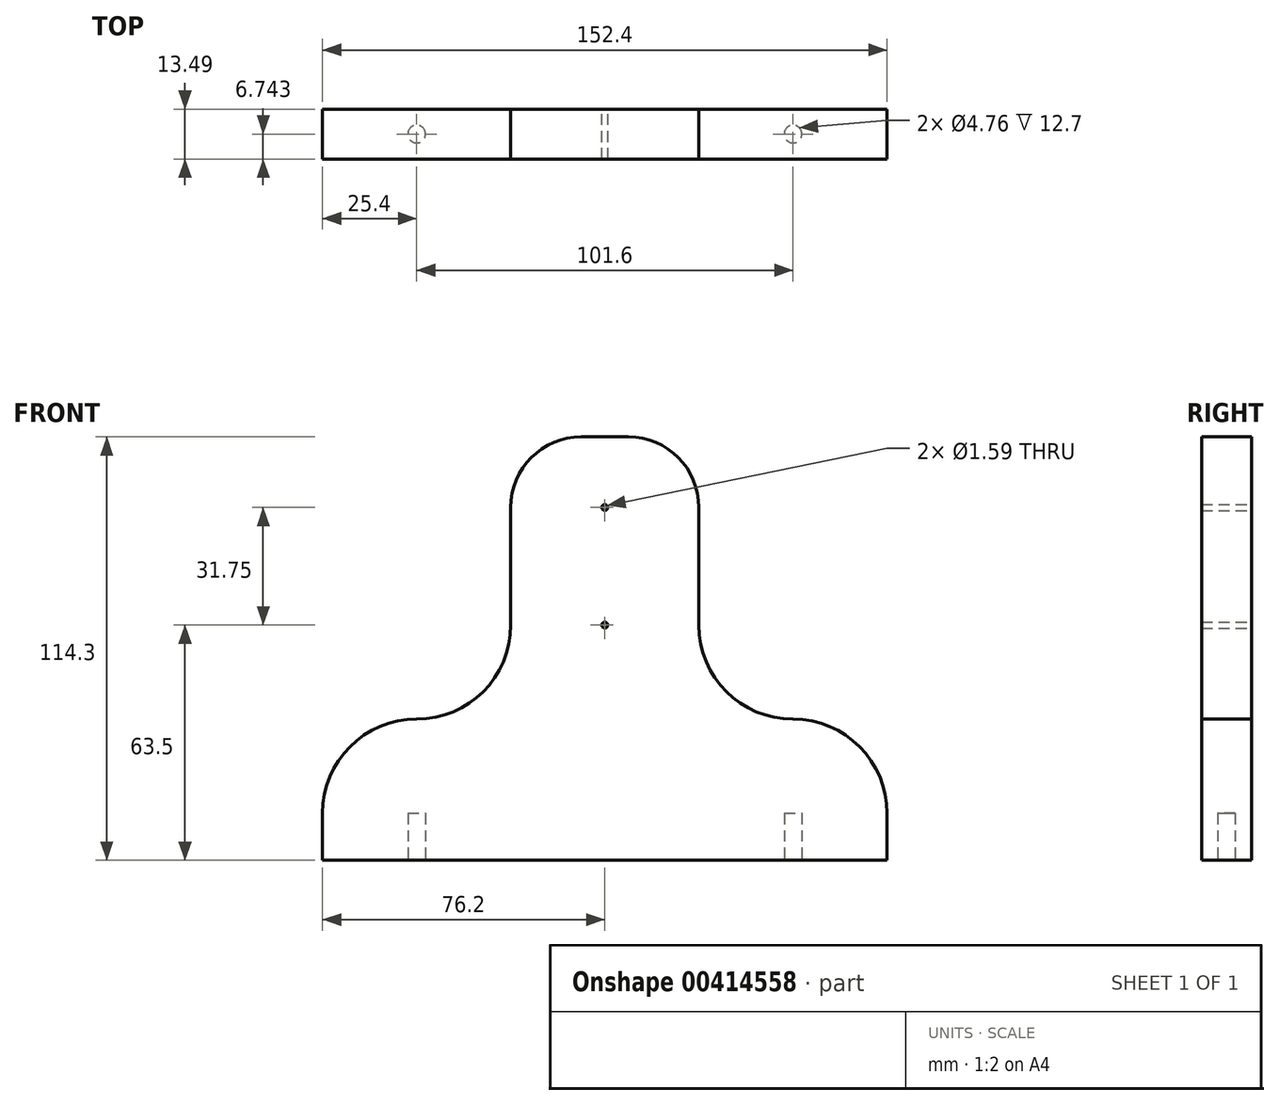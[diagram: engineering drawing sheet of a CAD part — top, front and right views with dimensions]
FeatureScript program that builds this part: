
annotation { "Feature Type Name" : "Feature", "Feature Type Description" : "" }
export const myFeature = defineFeature(function(context is Context, id is Id, definition is map)
    precondition{}
    {
        {
            var Q0;
            Q0=qCreatedBy(makeId("Front.planeOp"),FACE);
            var sketch = newSketch(context, id + "F0", { "sketchPlane" : qUnion([Q0])});
            skLineSegment(sketch, "E0", {"start": v(-76.2, 0) * mm, "end": v(76.2, 0) * mm});
            skLineSegment(sketch, "E1", {"start": v(76.2, 0) * mm, "end": v(76.2, 12.7) * mm});
            skLineSegment(sketch, "E2", {"start": v(50.8, 38.1) * mm, "end": v(50.8, 38.1) * mm});
            skLineSegment(sketch, "E3", {"start": v(25.4, 63.5) * mm, "end": v(25.4, 95.25) * mm});
            skLineSegment(sketch, "E4", {"start": v(6.35, 114.3) * mm, "end": v(-6.35, 114.3) * mm});
            skLineSegment(sketch, "E5", {"start": v(-25.4, 95.25) * mm, "end": v(-25.4, 63.5) * mm});
            skLineSegment(sketch, "E6", {"start": v(-50.8, 38.1) * mm, "end": v(-50.8, 38.1) * mm});
            skLineSegment(sketch, "E7", {"start": v(-76.2, 12.7) * mm, "end": v(-76.2, 0) * mm});
            skCircle(sketch, "E8", {"center": v(0, 95.25) * mm, "radius": 0.8 * mm});
            skCircle(sketch, "E9", {"center": v(0, 63.5) * mm, "radius": 0.8 * mm});
            skLineSegment(sketch, "E10", {"start": v(0, 114.3) * mm, "end": v(0, 0) * mm, "construction": true});
            skPoint(sketch, "E11.visualSharp", {"position": v(-25.4, 38.1) * mm});
            skArc(sketch, "E11.filletArc", {"start": v(-50.8, 38.1) * mm, "mid": v(-32.84, 45.54) * mm, "end": v(-25.4, 63.5) * mm});
            skPoint(sketch, "E12.visualSharp", {"position": v(25.4, 38.1) * mm});
            skArc(sketch, "E12.filletArc", {"start": v(25.4, 63.5) * mm, "mid": v(32.84, 45.54) * mm, "end": v(50.8, 38.1) * mm});
            skPoint(sketch, "E13.visualSharp", {"position": v(-76.2, 38.1) * mm});
            skArc(sketch, "E13.filletArc", {"start": v(-50.8, 38.1) * mm, "mid": v(-68.76, 30.66) * mm, "end": v(-76.2, 12.7) * mm});
            skPoint(sketch, "E14.visualSharp", {"position": v(76.2, 38.1) * mm});
            skArc(sketch, "E14.filletArc", {"start": v(76.2, 12.7) * mm, "mid": v(68.76, 30.66) * mm, "end": v(50.8, 38.1) * mm});
            skPoint(sketch, "E15.visualSharp", {"position": v(-25.4, 114.3) * mm});
            skArc(sketch, "E15.filletArc", {"start": v(-6.35, 114.3) * mm, "mid": v(-19.82, 108.72) * mm, "end": v(-25.4, 95.25) * mm});
            skPoint(sketch, "E16.visualSharp", {"position": v(25.4, 114.3) * mm});
            skArc(sketch, "E16.filletArc", {"start": v(25.4, 95.25) * mm, "mid": v(19.82, 108.72) * mm, "end": v(6.35, 114.3) * mm});
            skSolve(sketch);
        }
        {
            var Q0;
            Q0 = qSketchRegion(id + "F0", true);
            extrude(context, id + "F1", {"entities" : qUnion([Q0]), "depth" : 13.5 * mm});
        }
        {
            var Q0;
            Q0=makeQuery(id+"F1.opExtrude","SWEPT_FACE",FACE,{"disambiguationData":[OSD([sQuery(id+"F0.wireOp",EDGE,"E0")])]});
            var sketch = newSketch(context, id + "F2", { "sketchPlane" : qUnion([Q0])});
            skCircle(sketch, "E17", {"center": v(-50.8, 6.75) * mm, "radius": 2.38 * mm});
            skCircle(sketch, "E18", {"center": v(50.8, 6.75) * mm, "radius": 2.38 * mm});
            skLineSegment(sketch, "E19", {"start": v(-50.8, 6.75) * mm, "end": v(50.8, 6.75) * mm, "construction": true});
            skLineSegment(sketch, "E20", {"start": v(0, 0) * mm, "end": v(0, 6.75) * mm, "construction": true});
            skLineSegment(sketch, "E21", {"start": v(0, 6.75) * mm, "end": v(0, 13.5) * mm, "construction": true});
            skSolve(sketch);
        }
        {
            var Q0;
            Q0 = qSketchRegion(id + "F2", true);
            extrude(context, id + "F3", {"entities" : qUnion([Q0]), "operationType" : NewBodyOperationType.REMOVE, "oppositeDirection" : true, "depth" : 12.7 * mm});
        }
    });
